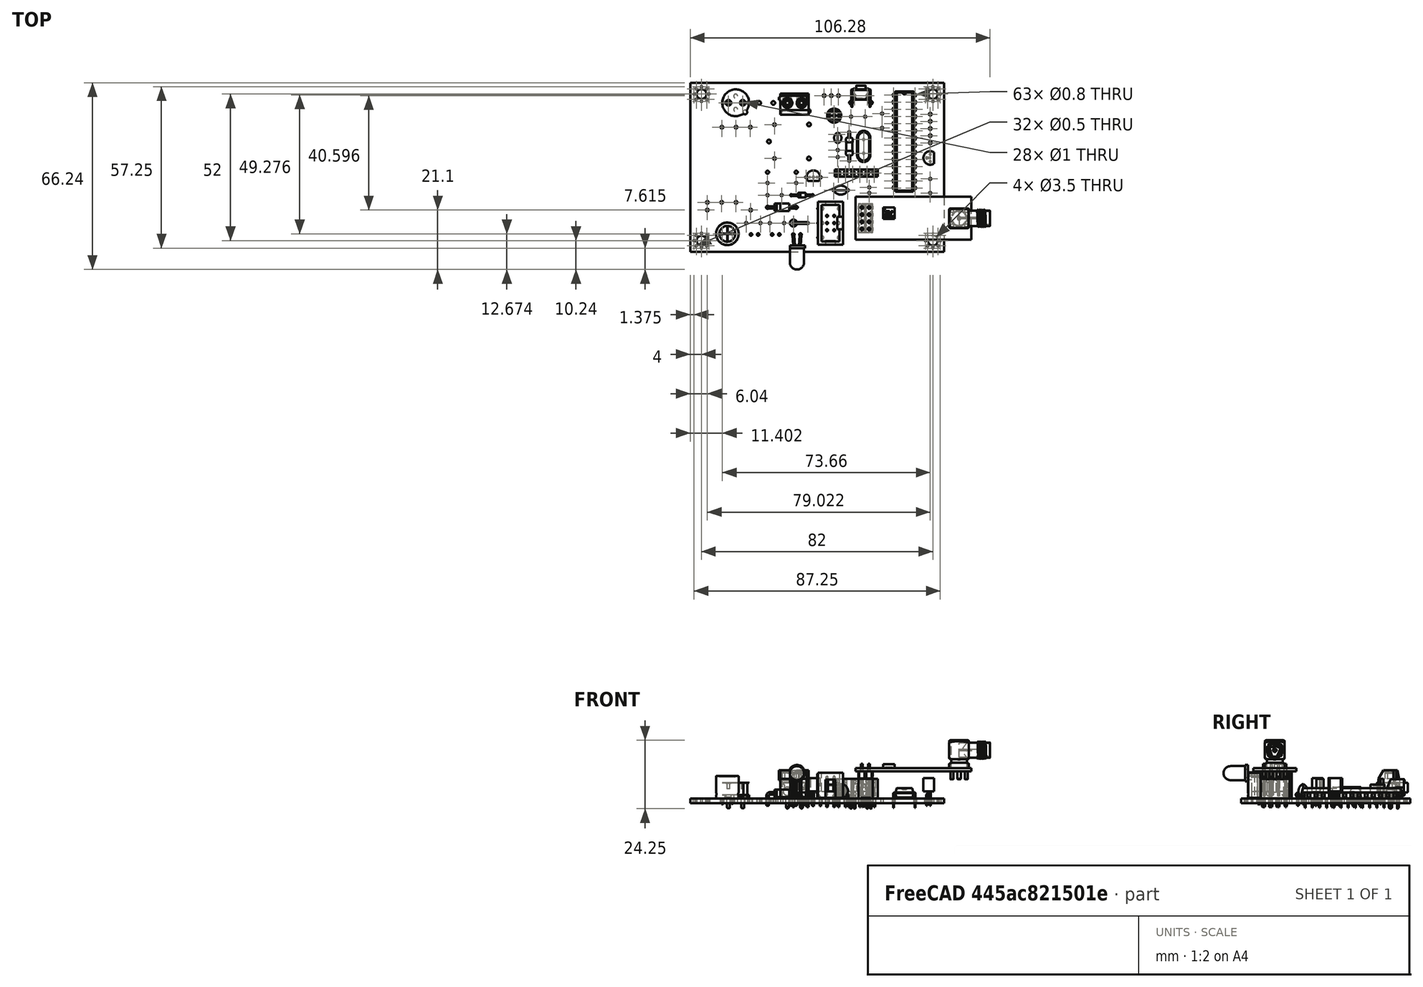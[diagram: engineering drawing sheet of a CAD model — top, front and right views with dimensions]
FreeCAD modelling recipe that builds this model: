
FCSTD DOCUMENT  (FreeCAD 0.19R)
Label: atmega328
License: All rights reserved
LicenseURL: http://en.wikipedia.org/wiki/All_rights_reserved
objects: Part::Feature×21, App::Link×13, App::Part×4, PartDesign::CoordinateSystem×1, Sketcher::SketchObject×1
note: 23 computed .brp shape members not serialized (recipe doc carries the construction recipe); baked Part::Feature solids carry a one-line shape summary decoded from their .brp

FEATURE [PartDesign::CoordinateSystem] Local_CS_f059
  AttacherType = Attacher::AttachEngine3D
FEATURE [Part::Feature] Pcb_f059
  shape: bbox 90 x 60 x 1.6 mm, 171 faces (baked)
FEATURE [Sketcher::SketchObject] PCB_Sketch_f059
  sketch-geometry (4):
    g0: LineSegment StartX=190 StartY=-65 StartZ=0 EndX=190 EndY=-125 EndZ=0
    g1: LineSegment StartX=100 StartY=-125 StartZ=0 EndX=100 EndY=-65 EndZ=0
    g2: LineSegment StartX=100 StartY=-125 StartZ=0 EndX=190 EndY=-125 EndZ=0
    g3: LineSegment StartX=100 StartY=-65 StartZ=0 EndX=190 EndY=-65 EndZ=0
  constraints (4):
    c: Coincident(g1,g2)
    c: Coincident(g1,g3)
    c: Coincident(g0,g2)
    c: Coincident(g0,g3)
FEATURE [App::Part] Board_Geoms_f059
  Group = -> [Local_CS_f059,Pcb_f059,PCB_Sketch_f059]
  Origin = -> Origin
FEATURE [Part::Feature] Shape  label="C8_CP_Radial_D50mm_P200mm_5C228BFC"
  Placement = pos=(151,-75.64,0) rot=(0,0,-1;1.5708rad)
  shape: bbox 6.515 x 6.128 x 7 mm, 49 faces (baked)
FEATURE [App::Link] C8_CP_Radial_D50mm_P200mm_5C228BFC_ln_  label="C6_CP_Radial_D50mm_P200mm_5C228B3E"
  LinkPlacement = pos=(163.472,-104.088,0) rot=(0,0,1;1.5708rad)
  LinkedObject = -> Shape
  Placement = pos=(163.472,-104.088,0) rot=(0,0,1;1.5708rad)
FEATURE [Part::Feature] Shape001  label="D1_D_DO-41_SOD81_P10.16mm_Horizontal_5C228C1B"
  Placement = pos=(127.404,-109.168,0) rot=(0,0,1;0rad)
  shape: bbox 11.16 x 2.72 x 5.71 mm, 15 faces (baked)
FEATURE [Part::Feature] Shape002  label="C5_C_Disc_D51mm_W32mm_P500mm_5C2C32D8"
  Placement = pos=(155.852,-103.072,0) rot=(0,0,1;3.14159rad)
  shape: bbox 5.5 x 3.2 x 7.2 mm, 10 faces (baked)
FEATURE [Part::Feature] Shape003  label="J5_PinSocket_1x06_P254mm_Vertical_5C2BABEE"
  Placement = pos=(165.25,-97,0) rot=(0,0,-1;1.5708rad)
  shape: bbox 15.24 x 2.54 x 10.1 mm, 196 faces (baked)
FEATURE [Part::Feature] Shape004  label="Y1_Crystal_HC49-4H_Vertical_5C2673D7"
  Placement = pos=(161.476,-90,0) rot=(0,0,1;1.5708rad)
  shape: bbox 4.65 x 11.05 x 7 mm, 26 faces (baked)
FEATURE [App::Link] C5_C_Disc_D51mm_W32mm_P500mm_5C2C32D8_ln_  label="C9_C_Disc_D51mm_W32mm_P500mm_5C296A81"
  LinkPlacement = pos=(157,-77,0) rot=(0,0,1;0rad)
  LinkedObject = -> Shape002
  Placement = pos=(157,-77,0) rot=(0,0,1;0rad)
FEATURE [App::Link] C5_C_Disc_D51mm_W32mm_P500mm_5C2C32D8_ln_001  label="C7_C_Disc_D51mm_W32mm_P500mm_5C27EEF1"
  LinkPlacement = pos=(185.062,-104.088,0) rot=(0,0,1;1.5708rad)
  LinkedObject = -> Shape002
  Placement = pos=(185.062,-104.088,0) rot=(0,0,1;1.5708rad)
FEATURE [App::Link] C5_C_Disc_D51mm_W32mm_P500mm_5C2C32D8_ln_002  label="C3_C_Disc_D51mm_W32mm_P500mm_5C228AAA"
  LinkPlacement = pos=(127.404,-104.85,0) rot=(0,0,1;0rad)
  LinkedObject = -> Shape002
  Placement = pos=(127.404,-104.85,0) rot=(0,0,1;0rad)
FEATURE [Part::Feature] Shape005  label="C1_CP_Radial_D80mm_P350mm_5C22DB62"
  Placement = pos=(111.402,-118.566,0) rot=(0,0,1;0rad)
  shape: bbox 9.886 x 10.23 x 10 mm, 54 faces (baked)
FEATURE [Part::Feature] Shape006  label="U2_TO-92_Narrow_5C27EEBB"
  Placement = pos=(185.062,-92.912,0) rot=(0,0,1;1.5708rad)
  shape: bbox 3.745 x 4.83 x 9.8 mm, 23 faces (baked)
FEATURE [Part::Feature] Shape007  label="Q1_TO-92_Inline_Wide_5C2949E0"
  Placement = pos=(141.12,-98.5,0) rot=(0,0,1;0rad)
  shape: bbox 5.58 x 3.745 x 10 mm, 27 faces (baked)
FEATURE [Part::Feature] Shape008  label="J6_TE_1776244-008_sp_5C2859B0"
  Placement = pos=(136.95,-72.15,0) rot=(0,0.707107,0.707107;3.14159rad)
  shape: bbox 11.16 x 7.501 x 13.5 mm, 192 faces (baked)
FEATURE [App::Link] J6_TE_1776244_008_sp_5C2859B0_ln_  label="J1_TE_1776244-008_sp_5C287871"
  LinkPlacement = pos=(126.95,-72.15,0) rot=(0,0.707107,0.707107;3.14159rad)
  LinkedObject = -> Shape008
  Placement = pos=(126.95,-72.15,0) rot=(0,0.707107,0.707107;3.14159rad)
FEATURE [Part::Feature] Shape009  label="SW1_tactileswitch-right-angle-5mm_5C27D3F6[2]"
  Placement = pos=(160.5,-70.974,3.9) rot=(0,1,0;1.5708rad)
  shape: bbox 8.043 x 7.608 x 10.6 mm, 445 faces (baked)
FEATURE [Part::Feature] Shape010  label="J2_IDC_Header_2x03_P254mm_Vertical_5C228C8A"
  Placement = pos=(151,-117.296,0) rot=(0,0,1;3.14159rad)
  shape: bbox 9.1 x 15.28 x 12.1 mm, 150 faces (baked)
FEATURE [Part::Feature] Shape011  label="R5_R_Axial_DIN0207_L63mm_D25mm_P508mm_Vertical_5C26CE50"
  Placement = pos=(136.58,-114.756,0) rot=(0,0,1;0rad)
  shape: bbox 6.832 x 2.706 x 12.6 mm, 17 faces (baked)
FEATURE [App::Link] R5_R_Axial_DIN0207_L63mm_D25mm_P508mm_Vertical_5C26CE50_ln_  label="R4_R_Axial_DIN0207_L63mm_D25mm_P508mm_Vertical_5C26CE41"
  LinkPlacement = pos=(128.198,-114.756,0) rot=(0,0,1;0rad)
  LinkedObject = -> Shape011
  Placement = pos=(128.198,-114.756,0) rot=(0,0,1;0rad)
FEATURE [App::Link] R5_R_Axial_DIN0207_L63mm_D25mm_P508mm_Vertical_5C26CE50_ln_001  label="R3_R_Axial_DIN0207_L63mm_D25mm_P508mm_Vertical_5C26CE32"
  LinkPlacement = pos=(119.816,-114.756,0) rot=(0,0,1;0rad)
  LinkedObject = -> Shape011
  Placement = pos=(119.816,-114.756,0) rot=(0,0,1;0rad)
FEATURE [Part::Feature] Shape012  label="D5_LED_D5.0mm_Horizontal_O3.81mm_Z9.0mm_5C26CC1D"
  Placement = pos=(136.537,-118.825,0) rot=(0,0,1;0rad)
  shape: bbox 5.4 x 12.71 x 13.9 mm, 33 faces (baked)
FEATURE [App::Link] D5_LED_D5_0mm_Horizontal_O3_81mm_Z9_0mm_5C26CC1D_ln_  label="D4_LED_D5.0mm_Horizontal_O3.81mm_Z9.0mm_5C26CBF3"
  LinkPlacement = pos=(129.037,-118.825,0) rot=(0,0,1;0rad)
  LinkedObject = -> Shape012
  Placement = pos=(129.037,-118.825,0) rot=(0,0,1;0rad)
FEATURE [App::Link] D5_LED_D5_0mm_Horizontal_O3_81mm_Z9_0mm_5C26CC1D_ln_001  label="D3_LED_D5.0mm_Horizontal_O3.81mm_Z9.0mm_5C26CBC9"
  LinkPlacement = pos=(121.537,-118.825,0) rot=(0,0,1;0rad)
  LinkedObject = -> Shape012
  Placement = pos=(121.537,-118.825,0) rot=(0,0,1;0rad)
FEATURE [App::Link] D1_D_DO_41_SOD81_P10_16mm_Horizontal_5C228C1B_ln_  label="D2_D_DO-41_SOD81_P10.16mm_Horizontal_5C27A218"
  LinkPlacement = pos=(127.404,-96.722,0) rot=(0,0,1;0rad)
  LinkedObject = -> Shape001
  Placement = pos=(127.404,-96.722,0) rot=(0,0,1;0rad)
FEATURE [Part::Feature] Shape013  label="F1_A_Littelfuse_No560_No460_5C258DC7"
  Placement = pos=(113.561,-72.084,0) rot=(0,0,1;0rad)
  shape: bbox 9.5 x 9.5 x 9.03 mm, 35 faces (baked)
FEATURE [Part::Feature] Shape014  label="D6_D_DO-34_SOD68_P7.62mm_Horizontal_5C228C59"
  Placement = pos=(135.786,-104.85,0) rot=(0,0,1;0rad)
  shape: bbox 8.306 x 1.61 x 4.605 mm, 21 faces (baked)
FEATURE [Part::Feature] Shape015  label="C4_C_Disc_D38mm_W26mm_P250mm_5C228A95"
  Placement = pos=(152.296,-85.8,0) rot=(0,0,1;1.5708rad)
  shape: bbox 2.6 x 3.8 x 5.9 mm, 10 faces (baked)
FEATURE [App::Link] C4_C_Disc_D38mm_W26mm_P250mm_5C228A95_ln_  label="C2_C_Disc_D38mm_W26mm_P250mm_5C2289EC"
  LinkPlacement = pos=(152.296,-88.848,0) rot=(0,0,-1;1.5708rad)
  LinkedObject = -> Shape015
  Placement = pos=(152.296,-88.848,0) rot=(0,0,-1;1.5708rad)
FEATURE [App::Link] R5_R_Axial_DIN0207_L63mm_D25mm_P508mm_Vertical_5C26CE50_ln_002  label="R2_R_Axial_DIN0207_L63mm_D25mm_P508mm_Vertical_5C228D4F"
  LinkPlacement = pos=(168,-81,0) rot=(0,0,1;1.5708rad)
  LinkedObject = -> Shape011
  Placement = pos=(168,-81,0) rot=(0,0,1;1.5708rad)
FEATURE [Part::Feature] Shape016  label="R1_R_Axial_DIN0207_L63mm_D25mm_P1016mm_Horizontal_5C228D38"
  Placement = pos=(156.36,-82.53,0) rot=(0,0,-1;1.5708rad)
  shape: bbox 2.706 x 10.96 x 5.603 mm, 17 faces (baked)
FEATURE [App::Link] R1_R_Axial_DIN0207_L63mm_D25mm_P1016mm_Horizontal_5C228D38_ln_  label="R6_R_Axial_DIN0207_L63mm_D25mm_P1016mm_Horizontal_5C229971"
  LinkPlacement = pos=(127.404,-100.532,0) rot=(0,0,1;0rad)
  LinkedObject = -> Shape016
  Placement = pos=(127.404,-100.532,0) rot=(0,0,1;0rad)
FEATURE [Part::Feature] Shape017  label="U3_DIP-28_W7.62mm_5C27EC37"
  Placement = pos=(172.108,-69.29,0) rot=(0,0,1;0rad)
  shape: bbox 7.874 x 35.56 x 6.98 mm, 488 faces (baked)
FEATURE [Part::Feature] Shape018  label="U1_NRF24L01_PCB_sp_5C228DAA[2]"
  Placement = pos=(179.132,-113.068,9.6) rot=(0.57735,-0.57735,-0.57735;2.0944rad)
  shape: bbox 47.65 x 15.25 x 19.29 mm, 810 faces (baked)
FEATURE [Part::Feature] Shape019  label="U1_PinSocket_2x04_P254mm_Vertical_5C228DAA[3]"
  Placement = pos=(163.472,-109.168,0) rot=(0,0,1;0rad)
  shape: bbox 5.08 x 10.16 x 10.1 mm, 258 faces (baked)
FEATURE [App::Part] Top_f059
  Group = -> [Shape,C8_CP_Radial_D50mm_P200mm_5C228BFC_ln_,Shape001,Shape002,Shape003,Shape004,C5_C_Disc_D51mm_W32mm_P500mm_5C2C32D8_ln_,C5_C_Disc_D51mm_W32mm_P500mm_5C2C32D8_ln_001,C5_C_Disc_D51mm_W32mm_P500mm_5C2C32D8_ln_002,Shape005,Shape006,Shape007,Shape008,J6_TE_1776244_008_sp_5C2859B0_ln_,Shape009,Shape010,Shape011,R5_R_Axial_DIN0207_L63mm_D25mm_P508mm_Vertical_5C26CE50_ln_,+15 more]
  Origin = -> Origin003
FEATURE [App::Part] Step_Models_f059
  Group = -> [Top_f059]
  Origin = -> Origin002
FEATURE [App::Part] Board_f059  label="atmega328"
  Group = -> [Board_Geoms_f059,Step_Models_f059]
  Origin = -> Origin001
